# Revit family: Zumtobel ONICO-P L
name_source: partatom
category: Lighting Fixtures
revit_build: Autodesk Revit 2014 (Build: 20140709_2115(x64)
units: mm (PartAtom-declared; Revit-internal decimal feet)

## types (3) — shared parameters
Assembly Code = D5020200
Color Filter = 16777215
Description = ONICO L Pendant Luminaire
Dimming Lamp Color Temperature Shift = <None>
Emit Shape Visible in Rendering = No
Emit from Circle Diameter = 117 mm  [stored 0.383858 ft]
Lamp = LED
Manufacturer = Zumtobel Lighting
Tilt Angle = 90.00°
URL = http://www.zumtobel.com
Voltage = 230 V
Width = 132 mm  [stored 0.433071 ft]
zero-valued in all types: Default Elevation

## per-type parameters (varying)
| type | 3CV Track | Apparent Load | Height | Length | Model | Pendant | Photometric Web File | Tecton Track | Track Connection |
| ONIC-P L BS AN | No | 58 VA | 216 mm  [stored 0.708661 ft] | 132 mm  [stored 0.433071 ft] | 60510326 | Yes | ST8827.IES | No | No |
| ONIC-P L SCR 3CU | Yes | 36 VA | 216 mm  [stored 0.708661 ft] | 132 mm  [stored 0.433071 ft] | 60510348 | No | ST9026.IES | No | Yes |
| ONIC-P L BS TEC | No | 36 VA | 235 mm  [stored 0.770997 ft] | 162 mm  [stored 0.531496 ft] | 60510330 | No | ST8827.IES | Yes | Yes |

note: [stored X ft] marks values corroborated as IEEE doubles in the binary element streams (Revit-internal decimal feet)

## geometry (parser evidence)
native form markers: Sweep x1
no freeform markers — native parametric forms only
